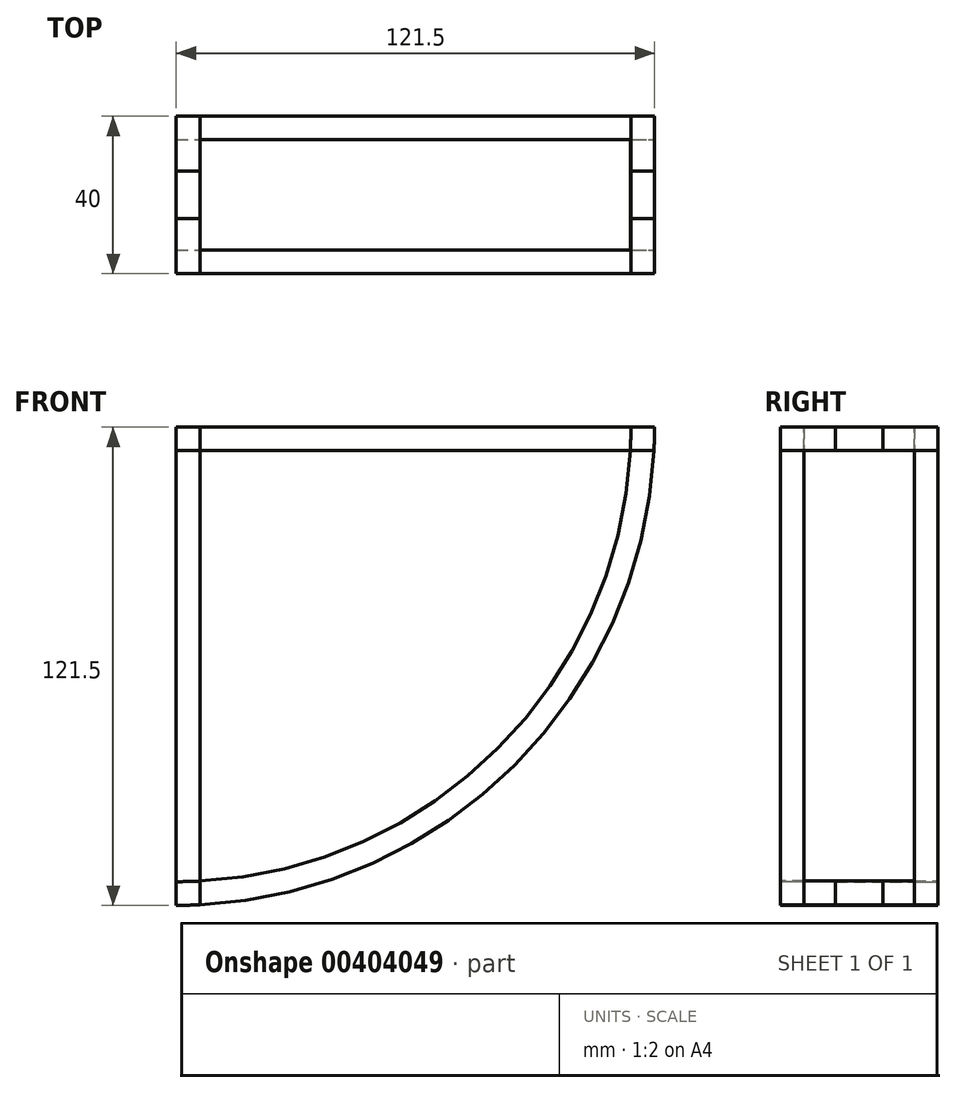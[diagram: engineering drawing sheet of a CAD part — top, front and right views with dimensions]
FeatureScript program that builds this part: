
annotation { "Feature Type Name" : "Feature", "Feature Type Description" : "" }
export const myFeature = defineFeature(function(context is Context, id is Id, definition is map)
    precondition{}
    {
        {
            var Q0;
            Q0=qCreatedBy(makeId("Front.planeOp"),FACE);
            var sketch = newSketch(context, id + "F0", { "sketchPlane" : qUnion([Q0])});
            skArc(sketch, "E0", {"start": v(0, -121.5) * mm, "mid": v(85.91, -85.91) * mm, "end": v(121.5, 0) * mm});
            skLineSegment(sketch, "E1", {"start": v(0, 0) * mm, "end": v(121.5, 0) * mm});
            skLineSegment(sketch, "E2", {"start": v(0, 0) * mm, "end": v(0, -121.5) * mm});
            skLineSegment(sketch, "E3.0", {"start": v(0, -6) * mm, "end": v(120, -6) * mm});
            skArc(sketch, "E4.0", {"start": v(0, -115.5) * mm, "mid": v(81.67, -81.67) * mm, "end": v(115.5, 0) * mm});
            skLineSegment(sketch, "E5.0", {"start": v(6, 0) * mm, "end": v(6, -120) * mm});
            skLineSegment(sketch, "E6", {"start": v(6, -120) * mm, "end": v(6, -121.35) * mm});
            skLineSegment(sketch, "E7", {"start": v(120, -6) * mm, "end": v(121.35, -6) * mm});
            skSolve(sketch);
        }
        {
            var Q0;
            {var subQ0=sQuery(id+"F0.wireOp",EDGE,"E2");var subQ1=sQuery(id+"F0.wireOp",EDGE,"E1");var subQ2=makeQuery(id+"F0.imprint","INTERSECT",VERTEX,{"derivedFrom":[subQ1,subQ0]});Q0=makeQuery(id+"F0.imprint","IMPRINT",FACE,{"disambiguationData":[TD([[makeQuery(id+"F0.imprint","IMPRINT",EDGE,{"disambiguationData":[TD([[subQ2,-1.0]])],"derivedFrom":subQ1}),-1.0]])]});}
            var Q1;
            {var subQ0=sQuery(id+"F0.wireOp",EDGE,"E1");var subQ1=sQuery(id+"F0.wireOp",EDGE,"E0");var subQ2=makeQuery(id+"F0.imprint","INTERSECT",VERTEX,{"derivedFrom":[subQ1,subQ0]});Q1=makeQuery(id+"F0.imprint","IMPRINT",FACE,{"disambiguationData":[TD([[makeQuery(id+"F0.imprint","IMPRINT",EDGE,{"disambiguationData":[TD([[subQ2,1.0]])],"derivedFrom":subQ1}),1.0]])]});}
            var Q2;
            {var subQ0=sQuery(id+"F0.wireOp",EDGE,"E2");var subQ1=sQuery(id+"F0.wireOp",EDGE,"E0");var subQ2=makeQuery(id+"F0.imprint","INTERSECT",VERTEX,{"derivedFrom":[subQ1,subQ0]});Q2=makeQuery(id+"F0.imprint","IMPRINT",FACE,{"disambiguationData":[TD([[makeQuery(id+"F0.imprint","IMPRINT",EDGE,{"disambiguationData":[TD([[subQ2,-1.0]])],"derivedFrom":subQ1}),1.0]])]});}
            extrude(context, id + "F1", {"entities" : qUnion([Q0, Q1, Q2]), "depth" : 26 * mm});
        }
        {
            var Q0;
            {var subQ0=sQuery(id+"F0.wireOp",EDGE,"E4.0");var subQ1=sQuery(id+"F0.wireOp",EDGE,"E1");var subQ2=makeQuery(id+"F0.imprint","INTERSECT",VERTEX,{"derivedFrom":[subQ1,subQ0]});Q0=makeQuery(id+"F0.imprint","IMPRINT",FACE,{"disambiguationData":[TD([[makeQuery(id+"F0.imprint","IMPRINT",EDGE,{"disambiguationData":[TD([[subQ2,1.0]])],"derivedFrom":subQ1}),-1.0]])]});}
            var Q1;
            {var subQ0=sQuery(id+"F0.wireOp",EDGE,"E6");Q1=makeQuery(id+"F0.imprint","IMPRINT",FACE,{"disambiguationData":[TD([[makeQuery(id+"F0.imprint","IMPRINT",EDGE,{"derivedFrom":subQ0}),1.0]])]});}
            var Q2;
            {var subQ0=sQuery(id+"F0.wireOp",EDGE,"E3.0");var subQ1=sQuery(id+"F0.wireOp",EDGE,"E2");var subQ2=makeQuery(id+"F0.imprint","INTERSECT",VERTEX,{"derivedFrom":[subQ1,subQ0]});Q2=makeQuery(id+"F0.imprint","IMPRINT",FACE,{"disambiguationData":[TD([[makeQuery(id+"F0.imprint","IMPRINT",EDGE,{"disambiguationData":[TD([[subQ2,-1.0]])],"derivedFrom":subQ1}),1.0]])]});}
            extrude(context, id + "F2", {"entities" : qUnion([Q0, Q1, Q2]), "depth" : 6 * mm});
        }
        {
            var Q0;
            Q0=makeQuery(id+"F1.opExtrude","SWEPT_BODY",BODY,{"disambiguationData":[OSD([sQuery(id+"F0.wireOp",EDGE,"E0"),sQuery(id+"F0.wireOp",EDGE,"E1"),sQuery(id+"F0.wireOp",EDGE,"E3.0"),sQuery(id+"F0.wireOp",EDGE,"E4.0")])]});
            var Q1;
            Q1=makeQuery(id+"F2.opExtrude","SWEPT_BODY",BODY,{"disambiguationData":[OSD([sQuery(id+"F0.wireOp",EDGE,"E0"),sQuery(id+"F0.wireOp",EDGE,"E3.0"),sQuery(id+"F0.wireOp",EDGE,"E4.0"),sQuery(id+"F0.wireOp",EDGE,"E5.0")])]});
            var Q2;
            Q2=makeQuery(id+"F1.opExtrude","SWEPT_BODY",BODY,{"disambiguationData":[OSD([sQuery(id+"F0.wireOp",EDGE,"E0"),sQuery(id+"F0.wireOp",EDGE,"E2"),sQuery(id+"F0.wireOp",EDGE,"E4.0"),sQuery(id+"F0.wireOp",EDGE,"E5.0")])]});
            var Q3;
            Q3=makeQuery(id+"F1.opExtrude","SWEPT_BODY",BODY,{"disambiguationData":[OSD([sQuery(id+"F0.wireOp",EDGE,"E1"),sQuery(id+"F0.wireOp",EDGE,"E2"),sQuery(id+"F0.wireOp",EDGE,"E3.0"),sQuery(id+"F0.wireOp",EDGE,"E5.0")])]});
            var Q4;
            Q4=makeQuery(id+"F2.opExtrude","SWEPT_BODY",BODY,{"disambiguationData":[OSD([sQuery(id+"F0.wireOp",EDGE,"E1"),sQuery(id+"F0.wireOp",EDGE,"E3.0"),sQuery(id+"F0.wireOp",EDGE,"E4.0"),sQuery(id+"F0.wireOp",EDGE,"E5.0")])]});
            var Q5;
            Q5=makeQuery(id+"F2.opExtrude","SWEPT_BODY",BODY,{"disambiguationData":[OSD([sQuery(id+"F0.wireOp",EDGE,"E2"),sQuery(id+"F0.wireOp",EDGE,"E3.0"),sQuery(id+"F0.wireOp",EDGE,"E4.0"),sQuery(id+"F0.wireOp",EDGE,"E5.0")])]});
            transform(context, id + "F3", {"entities" : qUnion([Q0, Q1, Q2, Q3, Q4, Q5]), "transformType" : TransformType.TRANSLATION_3D, "dx" : 0 * mm, "dy" : 20 * mm, "dz" : 0 * mm, "makeCopy" : false});
        }
        {
            var Q0;
            Q0=makeQuery(id+"F1.opExtrude","SWEPT_BODY",BODY,{"disambiguationData":[OSD([sQuery(id+"F0.wireOp",EDGE,"E0"),sQuery(id+"F0.wireOp",EDGE,"E2"),sQuery(id+"F0.wireOp",EDGE,"E4.0"),sQuery(id+"F0.wireOp",EDGE,"E5.0")])]});
            var Q1;
            Q1=makeQuery(id+"F2.opExtrude","SWEPT_BODY",BODY,{"disambiguationData":[OSD([sQuery(id+"F0.wireOp",EDGE,"E1"),sQuery(id+"F0.wireOp",EDGE,"E3.0"),sQuery(id+"F0.wireOp",EDGE,"E4.0"),sQuery(id+"F0.wireOp",EDGE,"E5.0")])]});
            var Q2;
            Q2=makeQuery(id+"F2.opExtrude","SWEPT_BODY",BODY,{"disambiguationData":[OSD([sQuery(id+"F0.wireOp",EDGE,"E2"),sQuery(id+"F0.wireOp",EDGE,"E3.0"),sQuery(id+"F0.wireOp",EDGE,"E4.0"),sQuery(id+"F0.wireOp",EDGE,"E5.0")])]});
            var Q3;
            Q3=makeQuery(id+"F1.opExtrude","SWEPT_BODY",BODY,{"disambiguationData":[OSD([sQuery(id+"F0.wireOp",EDGE,"E1"),sQuery(id+"F0.wireOp",EDGE,"E2"),sQuery(id+"F0.wireOp",EDGE,"E3.0"),sQuery(id+"F0.wireOp",EDGE,"E5.0")])]});
            var Q4;
            Q4=makeQuery(id+"F2.opExtrude","SWEPT_BODY",BODY,{"disambiguationData":[OSD([sQuery(id+"F0.wireOp",EDGE,"E0"),sQuery(id+"F0.wireOp",EDGE,"E3.0"),sQuery(id+"F0.wireOp",EDGE,"E4.0"),sQuery(id+"F0.wireOp",EDGE,"E5.0")])]});
            var Q5;
            Q5=makeQuery(id+"F1.opExtrude","SWEPT_BODY",BODY,{"disambiguationData":[OSD([sQuery(id+"F0.wireOp",EDGE,"E0"),sQuery(id+"F0.wireOp",EDGE,"E1"),sQuery(id+"F0.wireOp",EDGE,"E3.0"),sQuery(id+"F0.wireOp",EDGE,"E4.0")])]});
            var Q6;
            Q6=qCreatedBy(makeId("Front.planeOp"),FACE);
            mirror(context, id + "F4", {"entities" : qUnion([Q0, Q1, Q2, Q3, Q4, Q5]), "mirrorPlane" : qUnion([Q6])});
        }
    });
